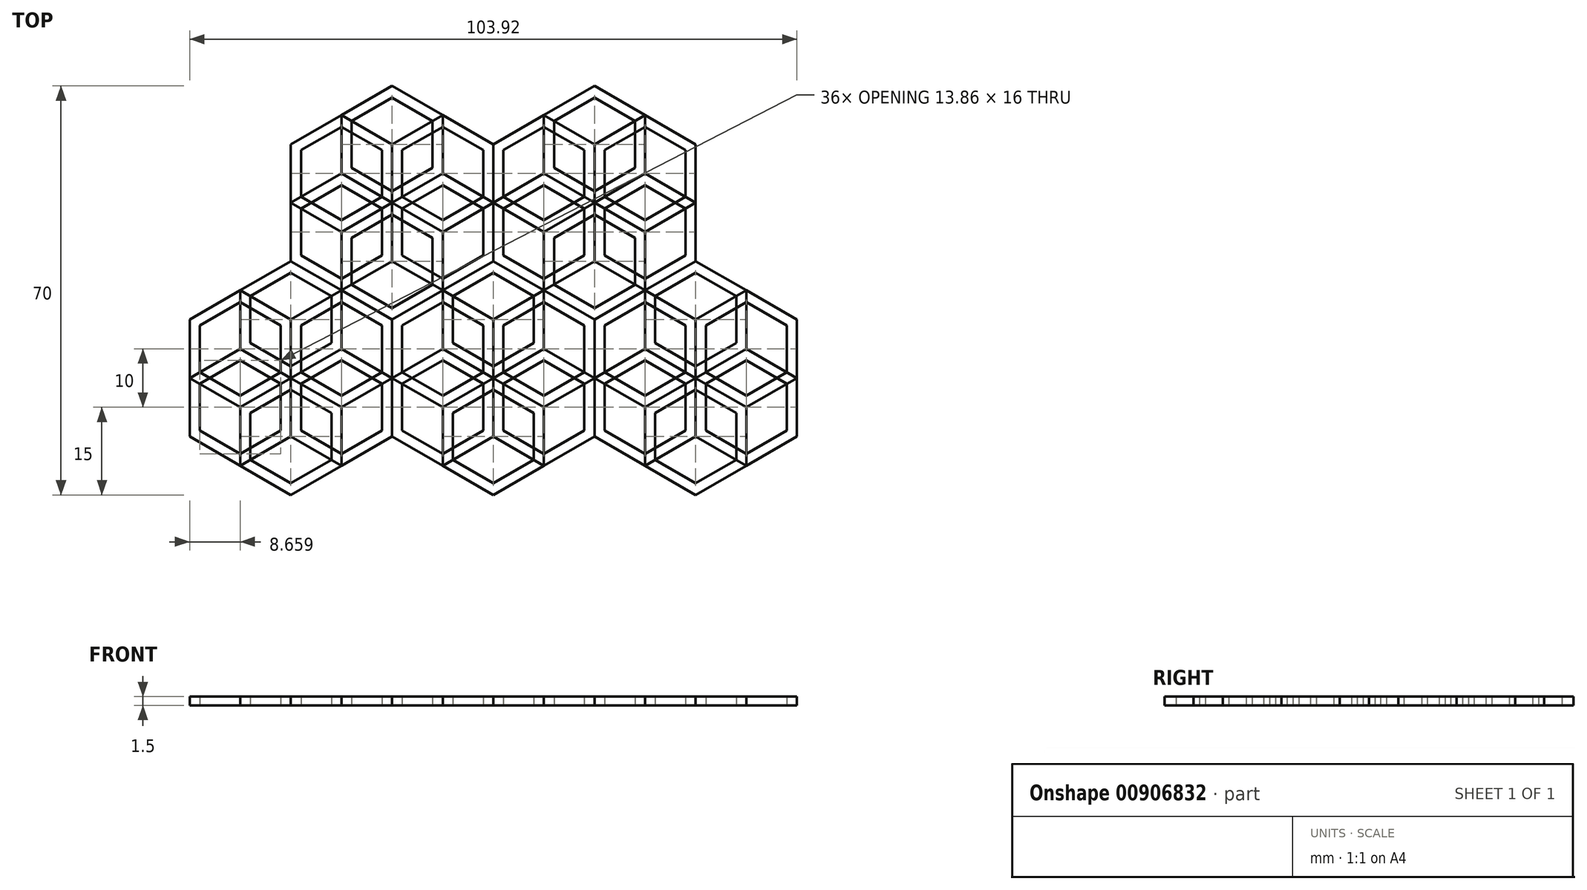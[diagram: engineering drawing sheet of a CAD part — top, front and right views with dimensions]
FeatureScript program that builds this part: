
annotation { "Feature Type Name" : "Feature", "Feature Type Description" : "" }
export const myFeature = defineFeature(function(context is Context, id is Id, definition is map)
    precondition{}
    {
        {
            var Q0;
            Q0=qCreatedBy(makeId("Top.planeOp"),FACE);
            var sketch = newSketch(context, id + "F0", { "sketchPlane" : qUnion([Q0])});
            skCircle(sketch, "E0.cCircle", {"center": v(0, 0) * mm, "radius": 8 * mm, "construction": true});
            skLineSegment(sketch, "E0.0", {"start": v(0, 8) * mm, "end": v(6.93, 4) * mm});
            skLineSegment(sketch, "E0.1", {"start": v(6.93, 4) * mm, "end": v(6.93, -4) * mm});
            skLineSegment(sketch, "E0.2", {"start": v(6.93, -4) * mm, "end": v(0, -8) * mm});
            skLineSegment(sketch, "E0.3", {"start": v(0, -8) * mm, "end": v(-6.93, -4) * mm});
            skLineSegment(sketch, "E0.4", {"start": v(-6.93, -4) * mm, "end": v(-6.93, 4) * mm});
            skLineSegment(sketch, "E0.5", {"start": v(-6.93, 4) * mm, "end": v(0, 8) * mm});
            skCircle(sketch, "E1.cCircle", {"center": v(0, 0) * mm, "radius": 10 * mm, "construction": true});
            skLineSegment(sketch, "E1.0", {"start": v(0, -10) * mm, "end": v(-8.66, -5) * mm});
            skLineSegment(sketch, "E1.1", {"start": v(-8.66, -5) * mm, "end": v(-8.66, 5) * mm});
            skLineSegment(sketch, "E1.2", {"start": v(-8.66, 5) * mm, "end": v(0, 10) * mm});
            skLineSegment(sketch, "E1.3", {"start": v(0, 10) * mm, "end": v(8.66, 5) * mm});
            skLineSegment(sketch, "E1.4", {"start": v(8.66, 5) * mm, "end": v(8.66, -5) * mm});
            skLineSegment(sketch, "E1.5", {"start": v(8.66, -5) * mm, "end": v(0, -10) * mm});
            skSolve(sketch);
        }
        {
            var Q0;
            Q0=makeQuery(id+"F0.imprint","IMPRINT",FACE,{"disambiguationData":[TD([[makeQuery(id+"F0.imprint","IMPRINT",EDGE,{"derivedFrom":sQuery(id+"F0.wireOp",EDGE,"E0.0")}),1.0]])]});
            extrude(context, id + "F1", {"entities" : qUnion([Q0]), "depth" : 1.5 * mm, "offsetDistance" : 25 * mm});
        }
        {
            var Q0;
            Q0=makeQuery(id+"F1.opExtrude","SWEPT_BODY",BODY,{"disambiguationData":[OSD([sQuery(id+"F0.wireOp",EDGE,"E0.0"),sQuery(id+"F0.wireOp",EDGE,"E0.1"),sQuery(id+"F0.wireOp",EDGE,"E0.2"),sQuery(id+"F0.wireOp",EDGE,"E0.3"),sQuery(id+"F0.wireOp",EDGE,"E0.4"),sQuery(id+"F0.wireOp",EDGE,"E0.5"),sQuery(id+"F0.wireOp",EDGE,"E1.0"),sQuery(id+"F0.wireOp",EDGE,"E1.1"),sQuery(id+"F0.wireOp",EDGE,"E1.2"),sQuery(id+"F0.wireOp",EDGE,"E1.3"),sQuery(id+"F0.wireOp",EDGE,"E1.4"),sQuery(id+"F0.wireOp",EDGE,"E1.5")])]});
            var Q1;
            Q1=makeQuery(id+"F1.opExtrude","SWEPT_EDGE",EDGE,{"disambiguationData":[OSD([sQuery(id+"F0.wireOp",EDGE,"E1.3"),sQuery(id+"F0.wireOp",EDGE,"E1.4")])]});
            circularPattern(context, id + "F2", {"entities" : qUnion([Q0]), "axis" : qUnion([Q1]), "angle" : 360 * degree, "instanceCount" : 6, "equalSpace" : true});
        }
        {
            var Q0;
            Q0=makeQuery(id+"F1.opExtrude","SWEPT_BODY",BODY,{"disambiguationData":[OSD([sQuery(id+"F0.wireOp",EDGE,"E0.0"),sQuery(id+"F0.wireOp",EDGE,"E0.1"),sQuery(id+"F0.wireOp",EDGE,"E0.2"),sQuery(id+"F0.wireOp",EDGE,"E0.3"),sQuery(id+"F0.wireOp",EDGE,"E0.4"),sQuery(id+"F0.wireOp",EDGE,"E0.5"),sQuery(id+"F0.wireOp",EDGE,"E1.0"),sQuery(id+"F0.wireOp",EDGE,"E1.1"),sQuery(id+"F0.wireOp",EDGE,"E1.2"),sQuery(id+"F0.wireOp",EDGE,"E1.3"),sQuery(id+"F0.wireOp",EDGE,"E1.4"),sQuery(id+"F0.wireOp",EDGE,"E1.5")])]});
            var Q1;
            Q1=makeQuery(id+"F2.opPattern","COPY",BODY,{"derivedFrom":makeQuery(id+"F1.opExtrude","SWEPT_BODY",BODY,{"disambiguationData":[OSD([sQuery(id+"F0.wireOp",EDGE,"E0.0"),sQuery(id+"F0.wireOp",EDGE,"E0.1"),sQuery(id+"F0.wireOp",EDGE,"E0.2"),sQuery(id+"F0.wireOp",EDGE,"E0.3"),sQuery(id+"F0.wireOp",EDGE,"E0.4"),sQuery(id+"F0.wireOp",EDGE,"E0.5"),sQuery(id+"F0.wireOp",EDGE,"E1.0"),sQuery(id+"F0.wireOp",EDGE,"E1.1"),sQuery(id+"F0.wireOp",EDGE,"E1.2"),sQuery(id+"F0.wireOp",EDGE,"E1.3"),sQuery(id+"F0.wireOp",EDGE,"E1.4"),sQuery(id+"F0.wireOp",EDGE,"E1.5")])]}),"instanceName":"1"});
            var Q2;
            Q2=makeQuery(id+"F2.opPattern","COPY",BODY,{"derivedFrom":makeQuery(id+"F1.opExtrude","SWEPT_BODY",BODY,{"disambiguationData":[OSD([sQuery(id+"F0.wireOp",EDGE,"E0.0"),sQuery(id+"F0.wireOp",EDGE,"E0.1"),sQuery(id+"F0.wireOp",EDGE,"E0.2"),sQuery(id+"F0.wireOp",EDGE,"E0.3"),sQuery(id+"F0.wireOp",EDGE,"E0.4"),sQuery(id+"F0.wireOp",EDGE,"E0.5"),sQuery(id+"F0.wireOp",EDGE,"E1.0"),sQuery(id+"F0.wireOp",EDGE,"E1.1"),sQuery(id+"F0.wireOp",EDGE,"E1.2"),sQuery(id+"F0.wireOp",EDGE,"E1.3"),sQuery(id+"F0.wireOp",EDGE,"E1.4"),sQuery(id+"F0.wireOp",EDGE,"E1.5")])]}),"instanceName":"5"});
            var Q3;
            Q3=makeQuery(id+"F2.opPattern","COPY",BODY,{"derivedFrom":makeQuery(id+"F1.opExtrude","SWEPT_BODY",BODY,{"disambiguationData":[OSD([sQuery(id+"F0.wireOp",EDGE,"E0.0"),sQuery(id+"F0.wireOp",EDGE,"E0.1"),sQuery(id+"F0.wireOp",EDGE,"E0.2"),sQuery(id+"F0.wireOp",EDGE,"E0.3"),sQuery(id+"F0.wireOp",EDGE,"E0.4"),sQuery(id+"F0.wireOp",EDGE,"E0.5"),sQuery(id+"F0.wireOp",EDGE,"E1.0"),sQuery(id+"F0.wireOp",EDGE,"E1.1"),sQuery(id+"F0.wireOp",EDGE,"E1.2"),sQuery(id+"F0.wireOp",EDGE,"E1.3"),sQuery(id+"F0.wireOp",EDGE,"E1.4"),sQuery(id+"F0.wireOp",EDGE,"E1.5")])]}),"instanceName":"4"});
            var Q4;
            Q4=makeQuery(id+"F2.opPattern","COPY",BODY,{"derivedFrom":makeQuery(id+"F1.opExtrude","SWEPT_BODY",BODY,{"disambiguationData":[OSD([sQuery(id+"F0.wireOp",EDGE,"E0.0"),sQuery(id+"F0.wireOp",EDGE,"E0.1"),sQuery(id+"F0.wireOp",EDGE,"E0.2"),sQuery(id+"F0.wireOp",EDGE,"E0.3"),sQuery(id+"F0.wireOp",EDGE,"E0.4"),sQuery(id+"F0.wireOp",EDGE,"E0.5"),sQuery(id+"F0.wireOp",EDGE,"E1.0"),sQuery(id+"F0.wireOp",EDGE,"E1.1"),sQuery(id+"F0.wireOp",EDGE,"E1.2"),sQuery(id+"F0.wireOp",EDGE,"E1.3"),sQuery(id+"F0.wireOp",EDGE,"E1.4"),sQuery(id+"F0.wireOp",EDGE,"E1.5")])]}),"instanceName":"3"});
            var Q5;
            Q5=makeQuery(id+"F2.opPattern","COPY",BODY,{"derivedFrom":makeQuery(id+"F1.opExtrude","SWEPT_BODY",BODY,{"disambiguationData":[OSD([sQuery(id+"F0.wireOp",EDGE,"E0.0"),sQuery(id+"F0.wireOp",EDGE,"E0.1"),sQuery(id+"F0.wireOp",EDGE,"E0.2"),sQuery(id+"F0.wireOp",EDGE,"E0.3"),sQuery(id+"F0.wireOp",EDGE,"E0.4"),sQuery(id+"F0.wireOp",EDGE,"E0.5"),sQuery(id+"F0.wireOp",EDGE,"E1.0"),sQuery(id+"F0.wireOp",EDGE,"E1.1"),sQuery(id+"F0.wireOp",EDGE,"E1.2"),sQuery(id+"F0.wireOp",EDGE,"E1.3"),sQuery(id+"F0.wireOp",EDGE,"E1.4"),sQuery(id+"F0.wireOp",EDGE,"E1.5")])]}),"instanceName":"2"});
            var Q6;
            Q6=makeQuery(id+"F2.opPattern","COPY",EDGE,{"derivedFrom":makeQuery(id+"F1.opExtrude","SWEPT_EDGE",EDGE,{"disambiguationData":[OSD([sQuery(id+"F0.wireOp",EDGE,"E1.0"),sQuery(id+"F0.wireOp",EDGE,"E1.1")])]}),"instanceName":"3"});
            circularPattern(context, id + "F3", {"entities" : qUnion([Q0, Q1, Q2, Q3, Q4, Q5]), "axis" : qUnion([Q6]), "angle" : 360 * degree, "instanceCount" : 3, "equalSpace" : true});
        }
        {
            var Q0;
            Q0=makeQuery(id+"F1.opExtrude","SWEPT_BODY",BODY,{"disambiguationData":[OSD([sQuery(id+"F0.wireOp",EDGE,"E0.0"),sQuery(id+"F0.wireOp",EDGE,"E0.1"),sQuery(id+"F0.wireOp",EDGE,"E0.2"),sQuery(id+"F0.wireOp",EDGE,"E0.3"),sQuery(id+"F0.wireOp",EDGE,"E0.4"),sQuery(id+"F0.wireOp",EDGE,"E0.5"),sQuery(id+"F0.wireOp",EDGE,"E1.0"),sQuery(id+"F0.wireOp",EDGE,"E1.1"),sQuery(id+"F0.wireOp",EDGE,"E1.2"),sQuery(id+"F0.wireOp",EDGE,"E1.3"),sQuery(id+"F0.wireOp",EDGE,"E1.4"),sQuery(id+"F0.wireOp",EDGE,"E1.5")])]});
            var Q1;
            Q1=makeQuery(id+"F3.opPattern","COPY",BODY,{"derivedFrom":makeQuery(id+"F2.opPattern","COPY",BODY,{"derivedFrom":makeQuery(id+"F1.opExtrude","SWEPT_BODY",BODY,{"disambiguationData":[OSD([sQuery(id+"F0.wireOp",EDGE,"E0.0"),sQuery(id+"F0.wireOp",EDGE,"E0.1"),sQuery(id+"F0.wireOp",EDGE,"E0.2"),sQuery(id+"F0.wireOp",EDGE,"E0.3"),sQuery(id+"F0.wireOp",EDGE,"E0.4"),sQuery(id+"F0.wireOp",EDGE,"E0.5"),sQuery(id+"F0.wireOp",EDGE,"E1.0"),sQuery(id+"F0.wireOp",EDGE,"E1.1"),sQuery(id+"F0.wireOp",EDGE,"E1.2"),sQuery(id+"F0.wireOp",EDGE,"E1.3"),sQuery(id+"F0.wireOp",EDGE,"E1.4"),sQuery(id+"F0.wireOp",EDGE,"E1.5")])]}),"instanceName":"1"}),"instanceName":"1"});
            var Q2;
            Q2=makeQuery(id+"F2.opPattern","COPY",BODY,{"derivedFrom":makeQuery(id+"F1.opExtrude","SWEPT_BODY",BODY,{"disambiguationData":[OSD([sQuery(id+"F0.wireOp",EDGE,"E0.0"),sQuery(id+"F0.wireOp",EDGE,"E0.1"),sQuery(id+"F0.wireOp",EDGE,"E0.2"),sQuery(id+"F0.wireOp",EDGE,"E0.3"),sQuery(id+"F0.wireOp",EDGE,"E0.4"),sQuery(id+"F0.wireOp",EDGE,"E0.5"),sQuery(id+"F0.wireOp",EDGE,"E1.0"),sQuery(id+"F0.wireOp",EDGE,"E1.1"),sQuery(id+"F0.wireOp",EDGE,"E1.2"),sQuery(id+"F0.wireOp",EDGE,"E1.3"),sQuery(id+"F0.wireOp",EDGE,"E1.4"),sQuery(id+"F0.wireOp",EDGE,"E1.5")])]}),"instanceName":"1"});
            var Q3;
            Q3=makeQuery(id+"F3.opPattern","COPY",BODY,{"derivedFrom":makeQuery(id+"F1.opExtrude","SWEPT_BODY",BODY,{"disambiguationData":[OSD([sQuery(id+"F0.wireOp",EDGE,"E0.0"),sQuery(id+"F0.wireOp",EDGE,"E0.1"),sQuery(id+"F0.wireOp",EDGE,"E0.2"),sQuery(id+"F0.wireOp",EDGE,"E0.3"),sQuery(id+"F0.wireOp",EDGE,"E0.4"),sQuery(id+"F0.wireOp",EDGE,"E0.5"),sQuery(id+"F0.wireOp",EDGE,"E1.0"),sQuery(id+"F0.wireOp",EDGE,"E1.1"),sQuery(id+"F0.wireOp",EDGE,"E1.2"),sQuery(id+"F0.wireOp",EDGE,"E1.3"),sQuery(id+"F0.wireOp",EDGE,"E1.4"),sQuery(id+"F0.wireOp",EDGE,"E1.5")])]}),"instanceName":"1"});
            var Q4;
            Q4=makeQuery(id+"F2.opPattern","COPY",BODY,{"derivedFrom":makeQuery(id+"F1.opExtrude","SWEPT_BODY",BODY,{"disambiguationData":[OSD([sQuery(id+"F0.wireOp",EDGE,"E0.0"),sQuery(id+"F0.wireOp",EDGE,"E0.1"),sQuery(id+"F0.wireOp",EDGE,"E0.2"),sQuery(id+"F0.wireOp",EDGE,"E0.3"),sQuery(id+"F0.wireOp",EDGE,"E0.4"),sQuery(id+"F0.wireOp",EDGE,"E0.5"),sQuery(id+"F0.wireOp",EDGE,"E1.0"),sQuery(id+"F0.wireOp",EDGE,"E1.1"),sQuery(id+"F0.wireOp",EDGE,"E1.2"),sQuery(id+"F0.wireOp",EDGE,"E1.3"),sQuery(id+"F0.wireOp",EDGE,"E1.4"),sQuery(id+"F0.wireOp",EDGE,"E1.5")])]}),"instanceName":"5"});
            var Q5;
            Q5=makeQuery(id+"F2.opPattern","COPY",BODY,{"derivedFrom":makeQuery(id+"F1.opExtrude","SWEPT_BODY",BODY,{"disambiguationData":[OSD([sQuery(id+"F0.wireOp",EDGE,"E0.0"),sQuery(id+"F0.wireOp",EDGE,"E0.1"),sQuery(id+"F0.wireOp",EDGE,"E0.2"),sQuery(id+"F0.wireOp",EDGE,"E0.3"),sQuery(id+"F0.wireOp",EDGE,"E0.4"),sQuery(id+"F0.wireOp",EDGE,"E0.5"),sQuery(id+"F0.wireOp",EDGE,"E1.0"),sQuery(id+"F0.wireOp",EDGE,"E1.1"),sQuery(id+"F0.wireOp",EDGE,"E1.2"),sQuery(id+"F0.wireOp",EDGE,"E1.3"),sQuery(id+"F0.wireOp",EDGE,"E1.4"),sQuery(id+"F0.wireOp",EDGE,"E1.5")])]}),"instanceName":"4"});
            var Q6;
            Q6=makeQuery(id+"F2.opPattern","COPY",BODY,{"derivedFrom":makeQuery(id+"F1.opExtrude","SWEPT_BODY",BODY,{"disambiguationData":[OSD([sQuery(id+"F0.wireOp",EDGE,"E0.0"),sQuery(id+"F0.wireOp",EDGE,"E0.1"),sQuery(id+"F0.wireOp",EDGE,"E0.2"),sQuery(id+"F0.wireOp",EDGE,"E0.3"),sQuery(id+"F0.wireOp",EDGE,"E0.4"),sQuery(id+"F0.wireOp",EDGE,"E0.5"),sQuery(id+"F0.wireOp",EDGE,"E1.0"),sQuery(id+"F0.wireOp",EDGE,"E1.1"),sQuery(id+"F0.wireOp",EDGE,"E1.2"),sQuery(id+"F0.wireOp",EDGE,"E1.3"),sQuery(id+"F0.wireOp",EDGE,"E1.4"),sQuery(id+"F0.wireOp",EDGE,"E1.5")])]}),"instanceName":"3"});
            var Q7;
            Q7=makeQuery(id+"F3.opPattern","COPY",BODY,{"derivedFrom":makeQuery(id+"F2.opPattern","COPY",BODY,{"derivedFrom":makeQuery(id+"F1.opExtrude","SWEPT_BODY",BODY,{"disambiguationData":[OSD([sQuery(id+"F0.wireOp",EDGE,"E0.0"),sQuery(id+"F0.wireOp",EDGE,"E0.1"),sQuery(id+"F0.wireOp",EDGE,"E0.2"),sQuery(id+"F0.wireOp",EDGE,"E0.3"),sQuery(id+"F0.wireOp",EDGE,"E0.4"),sQuery(id+"F0.wireOp",EDGE,"E0.5"),sQuery(id+"F0.wireOp",EDGE,"E1.0"),sQuery(id+"F0.wireOp",EDGE,"E1.1"),sQuery(id+"F0.wireOp",EDGE,"E1.2"),sQuery(id+"F0.wireOp",EDGE,"E1.3"),sQuery(id+"F0.wireOp",EDGE,"E1.4"),sQuery(id+"F0.wireOp",EDGE,"E1.5")])]}),"instanceName":"4"}),"instanceName":"1"});
            var Q8;
            Q8=makeQuery(id+"F3.opPattern","COPY",BODY,{"derivedFrom":makeQuery(id+"F2.opPattern","COPY",BODY,{"derivedFrom":makeQuery(id+"F1.opExtrude","SWEPT_BODY",BODY,{"disambiguationData":[OSD([sQuery(id+"F0.wireOp",EDGE,"E0.0"),sQuery(id+"F0.wireOp",EDGE,"E0.1"),sQuery(id+"F0.wireOp",EDGE,"E0.2"),sQuery(id+"F0.wireOp",EDGE,"E0.3"),sQuery(id+"F0.wireOp",EDGE,"E0.4"),sQuery(id+"F0.wireOp",EDGE,"E0.5"),sQuery(id+"F0.wireOp",EDGE,"E1.0"),sQuery(id+"F0.wireOp",EDGE,"E1.1"),sQuery(id+"F0.wireOp",EDGE,"E1.2"),sQuery(id+"F0.wireOp",EDGE,"E1.3"),sQuery(id+"F0.wireOp",EDGE,"E1.4"),sQuery(id+"F0.wireOp",EDGE,"E1.5")])]}),"instanceName":"3"}),"instanceName":"1"});
            var Q9;
            Q9=makeQuery(id+"F3.opPattern","COPY",BODY,{"derivedFrom":makeQuery(id+"F2.opPattern","COPY",BODY,{"derivedFrom":makeQuery(id+"F1.opExtrude","SWEPT_BODY",BODY,{"disambiguationData":[OSD([sQuery(id+"F0.wireOp",EDGE,"E0.0"),sQuery(id+"F0.wireOp",EDGE,"E0.1"),sQuery(id+"F0.wireOp",EDGE,"E0.2"),sQuery(id+"F0.wireOp",EDGE,"E0.3"),sQuery(id+"F0.wireOp",EDGE,"E0.4"),sQuery(id+"F0.wireOp",EDGE,"E0.5"),sQuery(id+"F0.wireOp",EDGE,"E1.0"),sQuery(id+"F0.wireOp",EDGE,"E1.1"),sQuery(id+"F0.wireOp",EDGE,"E1.2"),sQuery(id+"F0.wireOp",EDGE,"E1.3"),sQuery(id+"F0.wireOp",EDGE,"E1.4"),sQuery(id+"F0.wireOp",EDGE,"E1.5")])]}),"instanceName":"2"}),"instanceName":"1"});
            var Q10;
            Q10=makeQuery(id+"F2.opPattern","COPY",BODY,{"derivedFrom":makeQuery(id+"F1.opExtrude","SWEPT_BODY",BODY,{"disambiguationData":[OSD([sQuery(id+"F0.wireOp",EDGE,"E0.0"),sQuery(id+"F0.wireOp",EDGE,"E0.1"),sQuery(id+"F0.wireOp",EDGE,"E0.2"),sQuery(id+"F0.wireOp",EDGE,"E0.3"),sQuery(id+"F0.wireOp",EDGE,"E0.4"),sQuery(id+"F0.wireOp",EDGE,"E0.5"),sQuery(id+"F0.wireOp",EDGE,"E1.0"),sQuery(id+"F0.wireOp",EDGE,"E1.1"),sQuery(id+"F0.wireOp",EDGE,"E1.2"),sQuery(id+"F0.wireOp",EDGE,"E1.3"),sQuery(id+"F0.wireOp",EDGE,"E1.4"),sQuery(id+"F0.wireOp",EDGE,"E1.5")])]}),"instanceName":"2"});
            var Q11;
            Q11=makeQuery(id+"F3.opPattern","COPY",BODY,{"derivedFrom":makeQuery(id+"F2.opPattern","COPY",BODY,{"derivedFrom":makeQuery(id+"F1.opExtrude","SWEPT_BODY",BODY,{"disambiguationData":[OSD([sQuery(id+"F0.wireOp",EDGE,"E0.0"),sQuery(id+"F0.wireOp",EDGE,"E0.1"),sQuery(id+"F0.wireOp",EDGE,"E0.2"),sQuery(id+"F0.wireOp",EDGE,"E0.3"),sQuery(id+"F0.wireOp",EDGE,"E0.4"),sQuery(id+"F0.wireOp",EDGE,"E0.5"),sQuery(id+"F0.wireOp",EDGE,"E1.0"),sQuery(id+"F0.wireOp",EDGE,"E1.1"),sQuery(id+"F0.wireOp",EDGE,"E1.2"),sQuery(id+"F0.wireOp",EDGE,"E1.3"),sQuery(id+"F0.wireOp",EDGE,"E1.4"),sQuery(id+"F0.wireOp",EDGE,"E1.5")])]}),"instanceName":"5"}),"instanceName":"1"});
            var Q12;
            Q12=makeQuery(id+"F3.opPattern","COPY",BODY,{"derivedFrom":makeQuery(id+"F1.opExtrude","SWEPT_BODY",BODY,{"disambiguationData":[OSD([sQuery(id+"F0.wireOp",EDGE,"E0.0"),sQuery(id+"F0.wireOp",EDGE,"E0.1"),sQuery(id+"F0.wireOp",EDGE,"E0.2"),sQuery(id+"F0.wireOp",EDGE,"E0.3"),sQuery(id+"F0.wireOp",EDGE,"E0.4"),sQuery(id+"F0.wireOp",EDGE,"E0.5"),sQuery(id+"F0.wireOp",EDGE,"E1.0"),sQuery(id+"F0.wireOp",EDGE,"E1.1"),sQuery(id+"F0.wireOp",EDGE,"E1.2"),sQuery(id+"F0.wireOp",EDGE,"E1.3"),sQuery(id+"F0.wireOp",EDGE,"E1.4"),sQuery(id+"F0.wireOp",EDGE,"E1.5")])]}),"instanceName":"2"});
            var Q13;
            Q13=makeQuery(id+"F3.opPattern","COPY",BODY,{"derivedFrom":makeQuery(id+"F2.opPattern","COPY",BODY,{"derivedFrom":makeQuery(id+"F1.opExtrude","SWEPT_BODY",BODY,{"disambiguationData":[OSD([sQuery(id+"F0.wireOp",EDGE,"E0.0"),sQuery(id+"F0.wireOp",EDGE,"E0.1"),sQuery(id+"F0.wireOp",EDGE,"E0.2"),sQuery(id+"F0.wireOp",EDGE,"E0.3"),sQuery(id+"F0.wireOp",EDGE,"E0.4"),sQuery(id+"F0.wireOp",EDGE,"E0.5"),sQuery(id+"F0.wireOp",EDGE,"E1.0"),sQuery(id+"F0.wireOp",EDGE,"E1.1"),sQuery(id+"F0.wireOp",EDGE,"E1.2"),sQuery(id+"F0.wireOp",EDGE,"E1.3"),sQuery(id+"F0.wireOp",EDGE,"E1.4"),sQuery(id+"F0.wireOp",EDGE,"E1.5")])]}),"instanceName":"1"}),"instanceName":"2"});
            var Q14;
            Q14=makeQuery(id+"F3.opPattern","COPY",BODY,{"derivedFrom":makeQuery(id+"F2.opPattern","COPY",BODY,{"derivedFrom":makeQuery(id+"F1.opExtrude","SWEPT_BODY",BODY,{"disambiguationData":[OSD([sQuery(id+"F0.wireOp",EDGE,"E0.0"),sQuery(id+"F0.wireOp",EDGE,"E0.1"),sQuery(id+"F0.wireOp",EDGE,"E0.2"),sQuery(id+"F0.wireOp",EDGE,"E0.3"),sQuery(id+"F0.wireOp",EDGE,"E0.4"),sQuery(id+"F0.wireOp",EDGE,"E0.5"),sQuery(id+"F0.wireOp",EDGE,"E1.0"),sQuery(id+"F0.wireOp",EDGE,"E1.1"),sQuery(id+"F0.wireOp",EDGE,"E1.2"),sQuery(id+"F0.wireOp",EDGE,"E1.3"),sQuery(id+"F0.wireOp",EDGE,"E1.4"),sQuery(id+"F0.wireOp",EDGE,"E1.5")])]}),"instanceName":"2"}),"instanceName":"2"});
            var Q15;
            Q15=makeQuery(id+"F3.opPattern","COPY",BODY,{"derivedFrom":makeQuery(id+"F2.opPattern","COPY",BODY,{"derivedFrom":makeQuery(id+"F1.opExtrude","SWEPT_BODY",BODY,{"disambiguationData":[OSD([sQuery(id+"F0.wireOp",EDGE,"E0.0"),sQuery(id+"F0.wireOp",EDGE,"E0.1"),sQuery(id+"F0.wireOp",EDGE,"E0.2"),sQuery(id+"F0.wireOp",EDGE,"E0.3"),sQuery(id+"F0.wireOp",EDGE,"E0.4"),sQuery(id+"F0.wireOp",EDGE,"E0.5"),sQuery(id+"F0.wireOp",EDGE,"E1.0"),sQuery(id+"F0.wireOp",EDGE,"E1.1"),sQuery(id+"F0.wireOp",EDGE,"E1.2"),sQuery(id+"F0.wireOp",EDGE,"E1.3"),sQuery(id+"F0.wireOp",EDGE,"E1.4"),sQuery(id+"F0.wireOp",EDGE,"E1.5")])]}),"instanceName":"3"}),"instanceName":"2"});
            var Q16;
            Q16=makeQuery(id+"F3.opPattern","COPY",BODY,{"derivedFrom":makeQuery(id+"F2.opPattern","COPY",BODY,{"derivedFrom":makeQuery(id+"F1.opExtrude","SWEPT_BODY",BODY,{"disambiguationData":[OSD([sQuery(id+"F0.wireOp",EDGE,"E0.0"),sQuery(id+"F0.wireOp",EDGE,"E0.1"),sQuery(id+"F0.wireOp",EDGE,"E0.2"),sQuery(id+"F0.wireOp",EDGE,"E0.3"),sQuery(id+"F0.wireOp",EDGE,"E0.4"),sQuery(id+"F0.wireOp",EDGE,"E0.5"),sQuery(id+"F0.wireOp",EDGE,"E1.0"),sQuery(id+"F0.wireOp",EDGE,"E1.1"),sQuery(id+"F0.wireOp",EDGE,"E1.2"),sQuery(id+"F0.wireOp",EDGE,"E1.3"),sQuery(id+"F0.wireOp",EDGE,"E1.4"),sQuery(id+"F0.wireOp",EDGE,"E1.5")])]}),"instanceName":"4"}),"instanceName":"2"});
            var Q17;
            Q17=makeQuery(id+"F3.opPattern","COPY",BODY,{"derivedFrom":makeQuery(id+"F2.opPattern","COPY",BODY,{"derivedFrom":makeQuery(id+"F1.opExtrude","SWEPT_BODY",BODY,{"disambiguationData":[OSD([sQuery(id+"F0.wireOp",EDGE,"E0.0"),sQuery(id+"F0.wireOp",EDGE,"E0.1"),sQuery(id+"F0.wireOp",EDGE,"E0.2"),sQuery(id+"F0.wireOp",EDGE,"E0.3"),sQuery(id+"F0.wireOp",EDGE,"E0.4"),sQuery(id+"F0.wireOp",EDGE,"E0.5"),sQuery(id+"F0.wireOp",EDGE,"E1.0"),sQuery(id+"F0.wireOp",EDGE,"E1.1"),sQuery(id+"F0.wireOp",EDGE,"E1.2"),sQuery(id+"F0.wireOp",EDGE,"E1.3"),sQuery(id+"F0.wireOp",EDGE,"E1.4"),sQuery(id+"F0.wireOp",EDGE,"E1.5")])]}),"instanceName":"5"}),"instanceName":"2"});
            var Q18;
            Q18=makeQuery(id+"F2.opPattern","COPY",EDGE,{"derivedFrom":makeQuery(id+"F1.opExtrude","SWEPT_EDGE",EDGE,{"disambiguationData":[OSD([sQuery(id+"F0.wireOp",EDGE,"E1.0"),sQuery(id+"F0.wireOp",EDGE,"E1.1")])]}),"instanceName":"2"});
            circularPattern(context, id + "F4", {"entities" : qUnion([Q0, Q1, Q2, Q3, Q4, Q5, Q6, Q7, Q8, Q9, Q10, Q11, Q12, Q13, Q14, Q15, Q16, Q17]), "axis" : qUnion([Q18]), "angle" : 120 * degree, "instanceCount" : 2, "equalSpace" : true});
        }
    });
